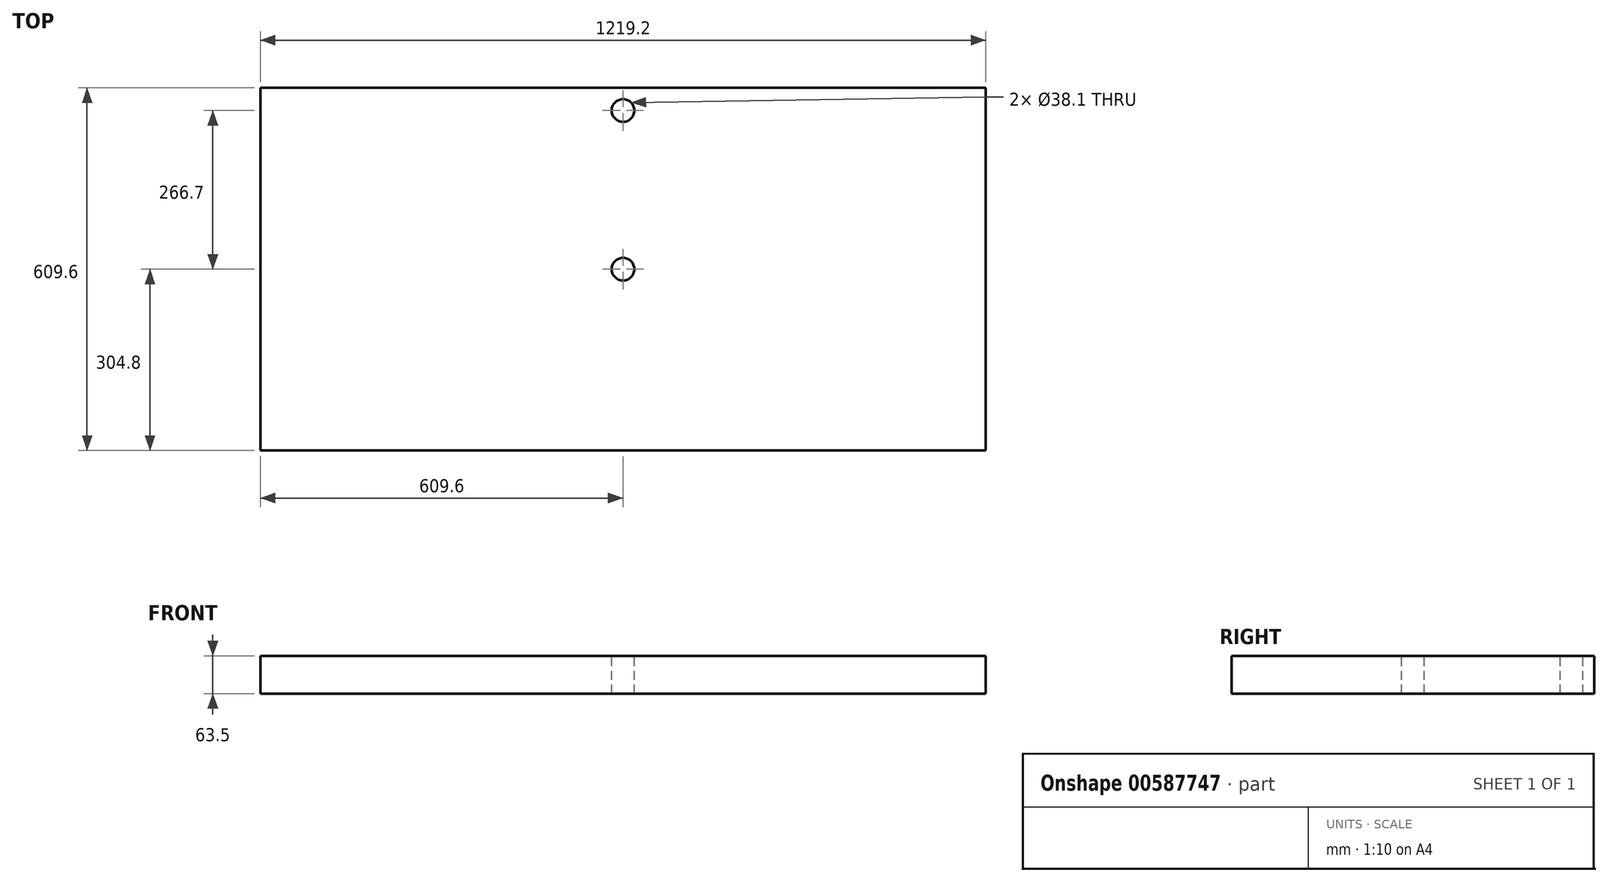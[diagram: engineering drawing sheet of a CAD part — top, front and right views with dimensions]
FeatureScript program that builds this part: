
annotation { "Feature Type Name" : "Feature", "Feature Type Description" : "" }
export const myFeature = defineFeature(function(context is Context, id is Id, definition is map)
    precondition{}
    {
        {
            var Q0;
            Q0=qCreatedBy(makeId("Front.planeOp"),FACE);
            var sketch = newSketch(context, id + "F0", { "sketchPlane" : qUnion([Q0])});
            skLineSegment(sketch, "E0.bottom", {"start": v(609.6, 31.75) * mm, "end": v(-609.6, 31.75) * mm});
            skLineSegment(sketch, "E0.top", {"start": v(609.6, -31.75) * mm, "end": v(-609.6, -31.75) * mm});
            skLineSegment(sketch, "E0.left", {"start": v(609.6, 31.75) * mm, "end": v(609.6, -31.75) * mm});
            skLineSegment(sketch, "E0.right", {"start": v(-609.6, 31.75) * mm, "end": v(-609.6, -31.75) * mm});
            skPoint(sketch, "E0.middle", {"position": v(0, 0) * mm});
            skSolve(sketch);
        }
        {
            var Q0;
            Q0=makeQuery(id+"F0.imprint","IMPRINT",FACE,{"disambiguationData":[TD([[makeQuery(id+"F0.imprint","IMPRINT",EDGE,{"derivedFrom":sQuery(id+"F0.wireOp",EDGE,"E0.bottom")}),1.0]])]});
            extrude(context, id + "F1", {"entities" : qUnion([Q0]), "endBound" : BoundingType.SYMMETRIC, "depth" : 609.6 * mm, "offsetDistance" : 25.4 * mm});
        }
        {
            var Q0;
            Q0=makeQuery(id+"F1.opExtrude","SWEPT_FACE",FACE,{"disambiguationData":[OSD([sQuery(id+"F0.wireOp",EDGE,"E0.bottom")])]});
            var sketch = newSketch(context, id + "F2", { "sketchPlane" : qUnion([Q0])});
            skCircle(sketch, "E1", {"center": v(0, 0) * mm, "radius": 19.05 * mm});
            skSolve(sketch);
        }
        {
            var Q0;
            Q0=makeQuery(id+"F2.imprint","IMPRINT",FACE,{"disambiguationData":[TD([[makeQuery(id+"F2.imprint","IMPRINT",EDGE,{"derivedFrom":sQuery(id+"F2.wireOp",EDGE,"E1")}),1.0]])]});
            extrude(context, id + "F3", {"entities" : qUnion([Q0]), "operationType" : NewBodyOperationType.REMOVE, "endBound" : BoundingType.THROUGH_ALL, "oppositeDirection" : true, "depth" : 25.4 * mm, "offsetDistance" : 25.4 * mm});
        }
        {
            var Q0;
            Q0=makeQuery(id+"F1.opExtrude","SWEPT_FACE",FACE,{"disambiguationData":[OSD([sQuery(id+"F0.wireOp",EDGE,"E0.bottom")])]});
            var sketch = newSketch(context, id + "F4", { "sketchPlane" : qUnion([Q0])});
            skLineSegment(sketch, "E2", {"start": v(0, 74.91) * mm, "end": v(0, 304.8) * mm, "construction": true});
            skLineSegment(sketch, "E3", {"start": v(-219.33, 266.7) * mm, "end": v(209.34, 266.7) * mm, "construction": true});
            skCircle(sketch, "E4", {"center": v(0, 266.7) * mm, "radius": 19.05 * mm});
            skSolve(sketch);
        }
        {
            var Q0;
            Q0=makeQuery(id+"F4.imprint","IMPRINT",FACE,{"disambiguationData":[TD([[makeQuery(id+"F4.imprint","IMPRINT",EDGE,{"derivedFrom":sQuery(id+"F4.wireOp",EDGE,"E4")}),1.0]])]});
            extrude(context, id + "F5", {"entities" : qUnion([Q0]), "operationType" : NewBodyOperationType.REMOVE, "endBound" : BoundingType.THROUGH_ALL, "oppositeDirection" : true, "depth" : 25.4 * mm, "offsetDistance" : 25.4 * mm});
        }
    });
